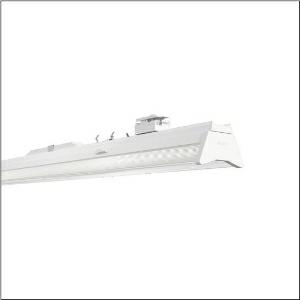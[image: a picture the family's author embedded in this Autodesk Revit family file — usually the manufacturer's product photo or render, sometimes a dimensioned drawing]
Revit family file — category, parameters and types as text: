
# Revit family: licross_r__21_performance_mo_52tm16cn46xg_6fd6
name_source: partatom
category: Lighting Fixtures
units: mm (PartAtom-declared; Revit-internal decimal feet)

## family parameters
Cut with Voids When Loaded = No
Host = Face
Light Source = No
Part Type = Normal
Room Calculation Point = No
Round Connector Dimension = Use Diameter
Shared = No

## types (1)
- --- (1 x LED, 6000 lm, 32 W, 4000K)
    Apparent Load = 32 VA
    CIE Flux Codes = 66 88 96 79 100
    Color Rendering = 80
    Color Temperature = 4000K
    Default Elevation = 1800 mm
    Description = Licross® 21 Performance MO, luminaire insert, of sheet steel, galvanised, coil coated, white, length: 1.500mm, width: 120mm, height: 123mm, LED rated luminous flux: 6.000lm, light colour: 840, control gear: ON/OFF Multilumen, CLOi, control gear: ECG Multilumen, with plug, 3-pole, with phase selection, mains connection: 220..240V, AC, 50/60Hz, start of lifetime: 32W, end of service life: 38W, internal wiring halogen-free, primary light control with lens, of plastic, primary optical cover: cover, of PMMA, light emission: direct/indirect distribution, primary light characteristic: symmetric, protection rating (complete): IP40, insulation class (complete): insulation class I (protective earthing), certification: CE, ENEC, UKCA, protection symbol: D if used in an environment without relevant dust loads with corresponding accessories, impact resistance: IK06, permissible ambient temperature for indoor applications: -35..+55°C, corresponds to IFS (International Featured Standards) requirements for safety and quality in the food industry, reducing of maximum allowable ambient temperature of 5°C with ceiling mounting, LABS conformity tested according to VDMA 24364:2018-05, packaging unit: 1 piece
    Height = 114 mm
    Lamp = 1 x LED
    Lamp Light Flux = 6000 lm
    Lamp Power = 32 W
    Lamp count = 1
    Length = 1500 mm
    Luminous efficacy = 188 lm/W
    Manufacturer = Siteco
    ModVariant = No
    Model = 52TM16CN46XG
    Mounting Place = Ceiling
    Mounting Type = Pendant
    Number of Poles = 1
    OnlyDefault = Yes
    Power Factor = 1
    Product Name = Licross® 21 Performance MO
    Product group = luminaire insert | ceiling pendant
    ProductGroupID = 902
    Protection Class = Protection class I
    Protection Degree = IP 40
    RLX_Detail_Level = 1
    RLX_Emergency_Light_Flux = 0 lm
    RLX_Emergency_Type = 0
    RLX_Emergency_Type_DB = No
    RlxData = <blob elided: 31869 chars, md5=191075d1>
    Socket = socket
    Standby Power = 0 W
    System Light Flux = 6000 lm
    System Power = 32 W
    Type Comments = factory setting: luminous flux: 100 % | (A | C | E) | 74 mA
    Type Image = l_1256138.jpg
    URL = http://relux.com
    VarID = @adj_133059
    Voltage = 0 V
    Weight = 0.00 kg
    Width = 120 mm

## geometry (parser evidence)
native form markers: Blend x4, Sweep x11
no freeform markers — native parametric forms only
